# Revit family: Resideo_VC-ValveBody_VCZM_1
name_source: partatom
category: Pipe Fittings
units: mm (PartAtom-declared; Revit-internal decimal feet)

## family parameters
Always vertical = Yes
Cut with Voids When Loaded = No
OmniClass Number = 23.65.55.14
OmniClass Title = Valves for Liquid Services
Part Type = Transition
Round Connector Dimension = Use Diameter
Shared = No
Work Plane-Based = No

## types (9) — shared parameters
Assembly Code = D20
AssetType = Fixed
BIMObjectName = Resideo_VC-ValveBody_VCZM
ClassificationName = Uniclass2015
ClassificationValue = Pr_65_54
Description = BODY VALVE
DocumentationCertificates = https://www.bimstore.co
DocumentationInstallationGuide = https://www.bimstore.co
DocumentationLiterature = https://www.bimstore.co
DocumentationMaintenance = https://www.bimstore.co
DocumentationTechnical = https://www.bimstore.co
DurationUnit = Year
IfcExportAs = IfcValve
IfcExportType = IfcValveTypeEnum.REGULATING
Keynote = S
Manufacturer = Resideo
ManufacturerName = Resideo
Material = Brass
MaximumDifferentialPressure = 4.0 bar
MaximumMediaTemperature = 95°C
MediumType = Water or water-glycol mixture according to VDI 2035
MinimumMediaTemperature = 1°C
ModelReference = BODY VALVE
NBSDescription = Valve products
NBSObjectName = Resideo - Valve products
NominalLength = 94 mm
NominalPressure = PN20
PrimaryMaterial = Resideo - Brass
ProductSeries = VC-M-int
ProductionYear = 2022
SecondaryMaterial = Resideo - Stainless Steel
Type Comments = BODY VALVE
URL = https://www.resideo.com
WarrantyDurationLabor = 0
WarrantyDurationParts = 0
WarrantyDurationUnit = Year
WarrantyGuarantorLabor = https://www.resideo.com
WarrantyGuarantorParts = https://www.resideo.com
_BSBibleVersion = 16
_CurrentRevision = 1
_DistributedBy = https://www.bimstore.co
_ObjectUserGuide = https://www.bimstore.co
d = 26.7 mm
zero-valued in all types: Cost, Default Elevation, ExpectedLife, _BimSpecGuid

## per-type parameters (varying)
- VCZMG6000: A=93.2 mm; ActuatorOffset=37 mm; Body1=Yes; Body2=Yes; ConnectionDia=20 mm  [stored 0.0656168 ft]; ConnectionRadius=10 mm  [stored 0.0328084 ft]; ConnectionSize=3/4"; ControlCharacteristics=On/Off; FlowCapacity(A-B)=6.6 m³/h; FlowCapacity(AB-B)=0.0 m³/h; NominalDepth=47 mm; NominalHeight=97 mm; Size=47mm (D) x 97mm (H) x 94mm (L); SpareParts=VC Series replacement cartridge for 3-port diverting valves, on/off [VCZZ6100/U]; VCZMH6000/U=No; VCZMH6100/U=No; VCZMP6000/U=No; VCZMU6000/U=No; Weight=0.42 kg; a=17.6 mm; b=37 mm; c=50.5 mm; e=3.2 mm; f=19.3 mm; g=18.3 mm; h=26.5 mm; i=37.9 mm
- VCZMG6100: A=93.2 mm; ActuatorOffset=37 mm; Body1=Yes; Body2=Yes; ConnectionDia=20 mm  [stored 0.0656168 ft]; ConnectionRadius=10 mm  [stored 0.0328084 ft]; ConnectionSize=3/4"; ControlCharacteristics=Modulating; FlowCapacity(A-B)=5.7 m³/h; FlowCapacity(AB-B)=0.0 m³/h; NominalDepth=47 mm; NominalHeight=97 mm; Size=47mm (D) x 97mm (H) x 94mm (L); SpareParts=VC Series replacement cartridge for 3-port diverting valves, on/off [VCZZ6100/U]; VCZMH6000/U=No; VCZMH6100/U=No; VCZMP6000/U=No; VCZMU6000/U=No; Weight=0.42 kg; a=19.5 mm; b=37 mm; c=50.5 mm; e=3.2 mm; f=19.3 mm; g=18.3 mm; h=26.5 mm; i=37.9 mm
- VCZMH6000: A=93.2 mm; ActuatorOffset=37 mm; Body1=No; Body2=Yes; ConnectionDia=20 mm  [stored 0.0656168 ft]; ConnectionRadius=10 mm  [stored 0.0328084 ft]; ConnectionSize=3/4"; ControlCharacteristics=On/Off; FlowCapacity(A-B)=6.6 m³/h; FlowCapacity(AB-B)=0.0 m³/h; NominalDepth=47 mm; NominalHeight=96 mm; Size=47mm (D) x 96mm (H) x 94mm (L); SpareParts=VC Series replacement cartridge for 3-port diverting valves, on/off [VCZZ6000/U]; VCZMH6000/U=Yes; VCZMH6100/U=No; VCZMP6000/U=No; VCZMU6000/U=No; Weight=0.55 kg; a=19.5 mm; b=37 mm; c=50.1 mm; e=3.2 mm; f=19.3 mm; g=18.3 mm; h=26.5 mm; i=37.9 mm
- VCZMH6100: A=93.2 mm; ActuatorOffset=37 mm; Body1=No; Body2=Yes; ConnectionDia=20 mm  [stored 0.0656168 ft]; ConnectionRadius=10 mm  [stored 0.0328084 ft]; ConnectionSize=3/4"; ControlCharacteristics=Modulating; FlowCapacity(A-B)=5.9 m³/h; FlowCapacity(AB-B)=0.0 m³/h; NominalDepth=47 mm; NominalHeight=96 mm; Size=47mm (D) x 96mm (H) x 94mm (L); SpareParts=VC Series replacement cartridge for 3-port diverting valves, on/off [VCZZ6100/U]; VCZMH6000/U=No; VCZMH6100/U=Yes; VCZMP6000/U=No; VCZMU6000/U=No; Weight=0.55 kg; a=17.6 mm; b=37 mm; c=50.1 mm; e=3.2 mm; f=19.3 mm; g=18.3 mm; h=26.5 mm; i=37.9 mm
- VCZMP6000: A=93.2 mm; ActuatorOffset=35 mm  [stored 0.114829 ft]; Body1=No; Body2=No; ConnectionDia=25 mm  [stored 0.082021 ft]; ConnectionRadius=12.5 mm  [stored 0.0410105 ft]; ConnectionSize=1"; ControlCharacteristics=On/Off; FlowCapacity(A-B)=8.5 m³/h; FlowCapacity(AB-B)=0.0 m³/h; NominalDepth=52 mm; NominalHeight=103 mm; Size=52mm (D) x 103mm (H) x 94mm (L); SpareParts=VC Series replacement cartridge for 3-port diverting valves, on/off [VCZZ6000/U]; VCZMH6000/U=No; VCZMH6100/U=No; VCZMP6000/U=Yes; VCZMU6000/U=No; Weight=0.62 kg; a=19.6 mm; b=35 mm  [stored 0.114829 ft]; c=49.6 mm; e=3.1 mm; f=13 mm; g=15.5 mm  [stored 0.050853 ft]; h=30 mm  [stored 0.0984252 ft]; i=45.5 mm
- VCZMP6100: A=93.2 mm; ActuatorOffset=35 mm  [stored 0.114829 ft]; Body1=No; Body2=No; ConnectionDia=25 mm  [stored 0.082021 ft]; ConnectionRadius=12.5 mm  [stored 0.0410105 ft]; ConnectionSize=1"; ControlCharacteristics=Modulating; FlowCapacity(A-B)=6.4 m³/h; FlowCapacity(AB-B)=0.0 m³/h; NominalDepth=52 mm; NominalHeight=103 mm; Size=52mm (D) x 103mm (H) x 94mm (L); SpareParts=VC Series replacement cartridge for 3-port diverting valves, on/off [VCZZ6100/U]; VCZMH6000/U=No; VCZMH6100/U=No; VCZMP6000/U=Yes; VCZMU6000/U=No; Weight=0.62 kg; a=19.6 mm; b=35 mm  [stored 0.114829 ft]; c=49.6 mm; e=3.1 mm; f=13 mm; g=15.5 mm  [stored 0.050853 ft]; h=30 mm  [stored 0.0984252 ft]; i=45.5 mm
- VCZMQ6100: A=93.2 mm; ActuatorOffset=35 mm  [stored 0.114829 ft]; Body1=No; Body2=No; ConnectionDia=25 mm  [stored 0.082021 ft]; ConnectionRadius=12.5 mm  [stored 0.0410105 ft]; ConnectionSize=1"; ControlCharacteristics=Modulating; FlowCapacity(A-B)=6.8 m³/h; FlowCapacity(AB-B)=0.0 m³/h; NominalDepth=52 mm; NominalHeight=103 mm; Size=52mm (D) x 103mm (H) x 94mm (L); SpareParts=VC Series replacement cartridge for 3-port diverting valves, on/off [VCZZ6100/U]; VCZMH6000/U=No; VCZMH6100/U=No; VCZMP6000/U=Yes; VCZMU6000/U=No; Weight=0.56 kg; a=19.6 mm; b=35 mm  [stored 0.114829 ft]; c=49.6 mm; e=3.1 mm; f=13 mm; g=15.5 mm  [stored 0.050853 ft]; h=30 mm  [stored 0.0984252 ft]; i=45.5 mm
- VCZMQ6000: A=93.2 mm; ActuatorOffset=35 mm  [stored 0.114829 ft]; Body1=No; Body2=No; ConnectionDia=25 mm  [stored 0.082021 ft]; ConnectionRadius=12.5 mm  [stored 0.0410105 ft]; ConnectionSize=1"; ControlCharacteristics=On/Off; FlowCapacity(A-B)=8.5 m³/h; FlowCapacity(AB-B)=0.0 m³/h; NominalDepth=52 mm; NominalHeight=103 mm; Size=52mm (D) x 103mm (H) x 94mm (L); SpareParts=VC Series replacement cartridge for 3-port diverting valves, on/off [VCZZ6000/U]; VCZMH6000/U=No; VCZMH6100/U=No; VCZMP6000/U=Yes; VCZMU6000/U=No; Weight=0.56 kg; a=19.6 mm; b=35 mm  [stored 0.114829 ft]; c=49.6 mm; e=3.1 mm; f=13 mm; g=15.5 mm  [stored 0.050853 ft]; h=30 mm  [stored 0.0984252 ft]; i=45.5 mm
- VCZMU6000: A=110 mm  [stored 0.360892 ft]; ActuatorOffset=27 mm  [stored 0.0885827 ft]; Body1=No; Body2=No; ConnectionDia=32 mm  [stored 0.104987 ft]; ConnectionRadius=16 mm  [stored 0.0524934 ft]; ConnectionSize=1 1/4"; ControlCharacteristics=On/Off; FlowCapacity(A-B)=8.5 m³/h; FlowCapacity(AB-B)=11.0 m³/h; NominalDepth=52 mm; NominalHeight=103 mm; Size=52mm (D) x 103mm (H) x 94mm (L); SpareParts=VC Series replacement cartridge for 3-port diverting valves, on/off [VCZZ6000/U]; VCZMH6000/U=No; VCZMH6100/U=No; VCZMP6000/U=No; VCZMU6000/U=Yes; Weight=0.00 kg; a=19.6 mm; b=35 mm  [stored 0.114829 ft]; c=49.6 mm; e=3.1 mm; f=13 mm; g=15.5 mm  [stored 0.050853 ft]; h=30 mm  [stored 0.0984252 ft]; i=47.5 mm

note: column(s) folded — value = type name in every type: Model, ModelNumber, TypeName

note: [stored X ft] marks values corroborated as IEEE doubles in the binary element streams (Revit-internal decimal feet)

## geometry (parser evidence)
native form markers: Sweep x3
no freeform markers — native parametric forms only
